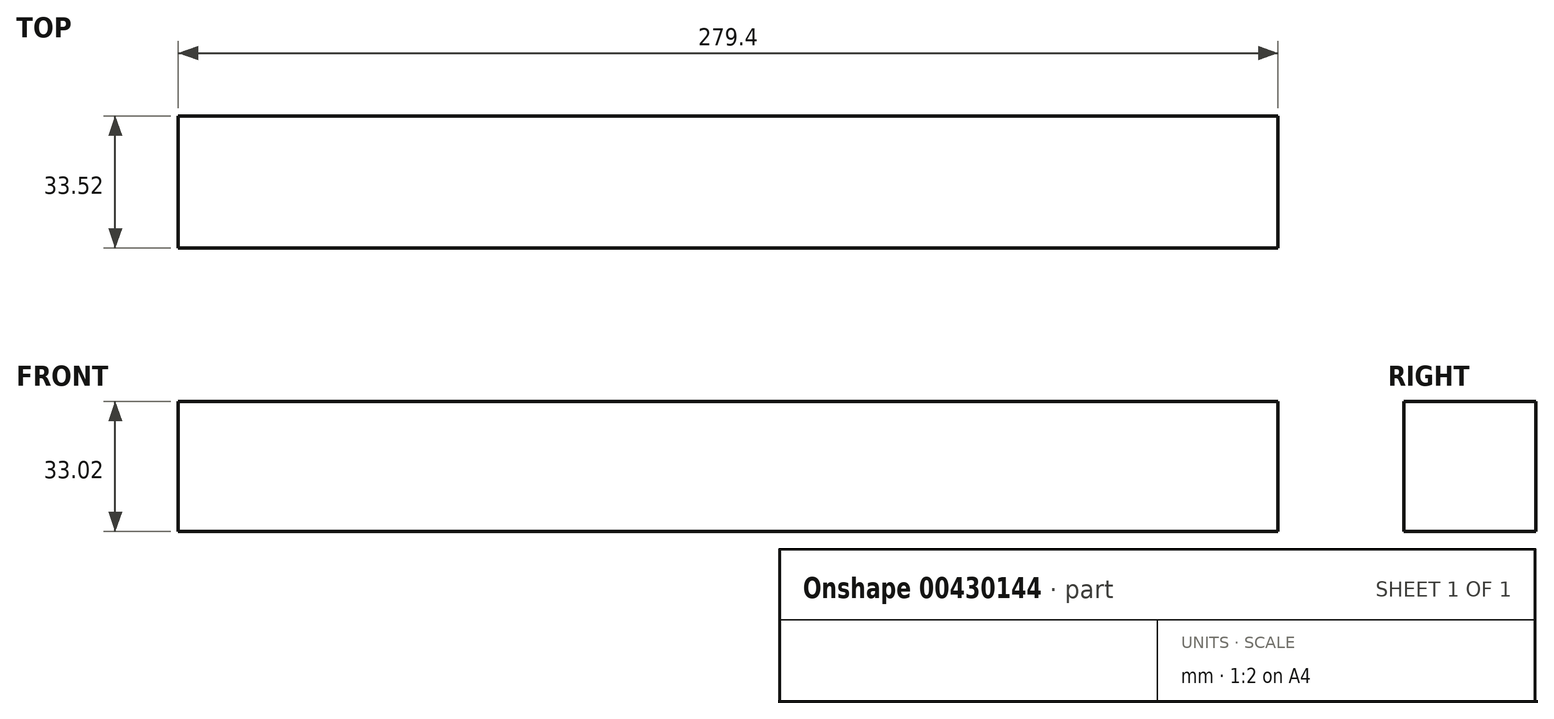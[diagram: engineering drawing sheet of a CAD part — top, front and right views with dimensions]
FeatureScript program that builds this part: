
annotation { "Feature Type Name" : "Feature", "Feature Type Description" : "" }
export const myFeature = defineFeature(function(context is Context, id is Id, definition is map)
    precondition{}
    {
        {
            var Q0;
            Q0=qCreatedBy(makeId("Top.planeOp"),FACE);
            var sketch = newSketch(context, id + "F0", { "sketchPlane" : qUnion([Q0])});
            skLineSegment(sketch, "E0.bottom", {"start": v(139.7, -16.76) * mm, "end": v(-139.7, -16.76) * mm});
            skLineSegment(sketch, "E0.top", {"start": v(139.7, 16.76) * mm, "end": v(-139.7, 16.76) * mm});
            skLineSegment(sketch, "E0.left", {"start": v(139.7, -16.76) * mm, "end": v(139.7, 16.76) * mm});
            skLineSegment(sketch, "E0.right", {"start": v(-139.7, -16.76) * mm, "end": v(-139.7, 16.76) * mm});
            skPoint(sketch, "E0.middle", {"position": v(0, 0) * mm});
            skSolve(sketch);
        }
        {
            var Q0;
            Q0 = qSketchRegion(id + "F0", true);
            extrude(context, id + "F1", {"entities" : qUnion([Q0]), "depth" : 33.02 * mm});
        }
    });
